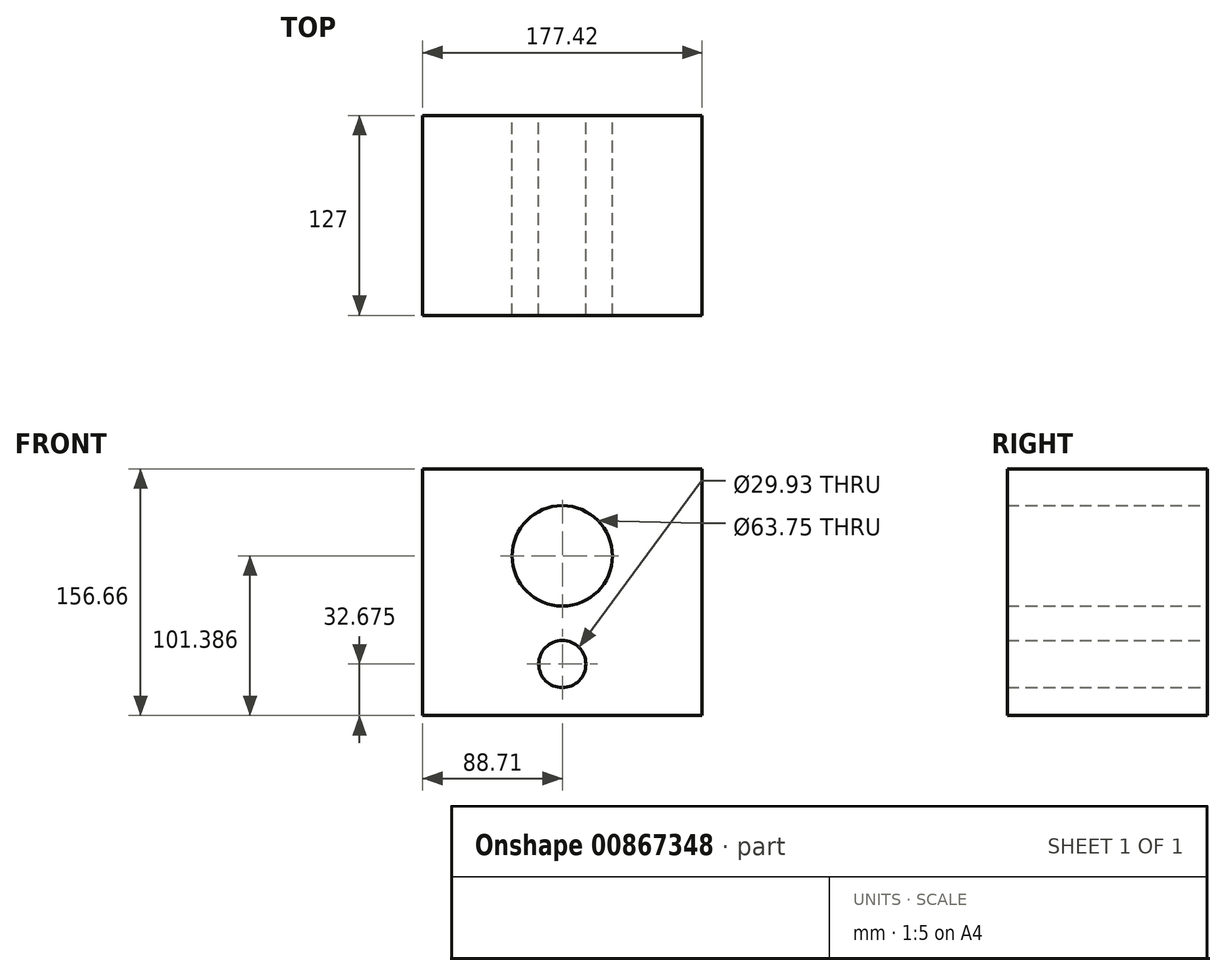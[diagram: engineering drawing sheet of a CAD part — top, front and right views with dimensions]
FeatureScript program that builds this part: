
annotation { "Feature Type Name" : "Feature", "Feature Type Description" : "" }
export const myFeature = defineFeature(function(context is Context, id is Id, definition is map)
    precondition{}
    {
        {
            var Q0;
            Q0=qCreatedBy(makeId("Front.planeOp"),FACE);
            var sketch = newSketch(context, id + "F0", { "sketchPlane" : qUnion([Q0])});
            skLineSegment(sketch, "E0.bottom", {"start": v(-88.71, 78.33) * mm, "end": v(88.71, 78.33) * mm});
            skLineSegment(sketch, "E0.top", {"start": v(-88.71, -78.33) * mm, "end": v(88.71, -78.33) * mm});
            skLineSegment(sketch, "E0.left", {"start": v(-88.71, 78.33) * mm, "end": v(-88.71, -78.33) * mm});
            skLineSegment(sketch, "E0.right", {"start": v(88.71, 78.33) * mm, "end": v(88.71, -78.33) * mm});
            skPoint(sketch, "E0.middle", {"position": v(0, 0) * mm});
            skCircle(sketch, "E1", {"center": v(0, -45.65) * mm, "radius": 14.96 * mm});
            skCircle(sketch, "E2", {"center": v(0, 23.06) * mm, "radius": 31.87 * mm});
            skSolve(sketch);
        }
        {
            var Q0;
            Q0 = qSketchRegion(id + "F0", true);
            extrude(context, id + "F1", {"entities" : qUnion([Q0]), "depth" : 127 * mm, "offsetDistance" : 25.4 * mm});
        }
    });
